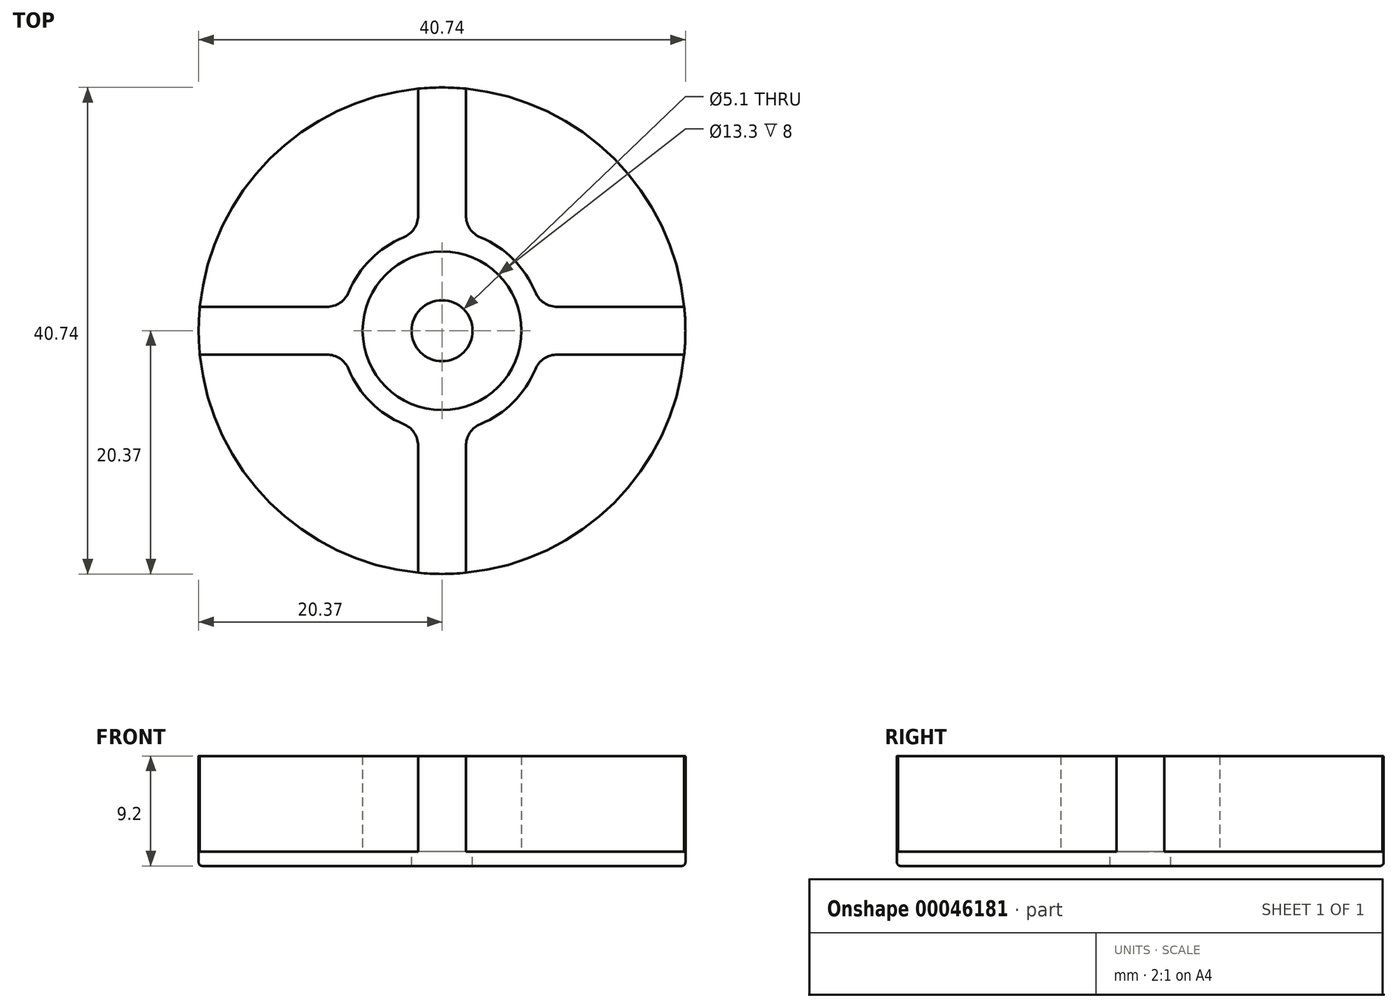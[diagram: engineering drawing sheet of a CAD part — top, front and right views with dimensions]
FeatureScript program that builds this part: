
annotation { "Feature Type Name" : "Feature", "Feature Type Description" : "" }
export const myFeature = defineFeature(function(context is Context, id is Id, definition is map)
    precondition{}
    {
        {
            var Q0;
            Q0=qCreatedBy(makeId("Top.planeOp"),FACE);
            var sketch = newSketch(context, id + "F0", { "sketchPlane" : qUnion([Q0])});
            skCircle(sketch, "E0", {"center": v(0, 0) * mm, "radius": 20.37 * mm});
            skLineSegment(sketch, "E1", {"start": v(0, 0) * mm, "end": v(0, 20.37) * mm, "construction": true});
            skLineSegment(sketch, "E2", {"start": v(0, 0) * mm, "end": v(2, 20.27) * mm, "construction": true});
            skLineSegment(sketch, "E3", {"start": v(7.8, 18.82) * mm, "end": v(0, 0) * mm, "construction": true});
            skLineSegment(sketch, "E4", {"start": v(0, 0) * mm, "end": v(14.4, 14.4) * mm, "construction": true});
            skLineSegment(sketch, "E5", {"start": v(2, 20.27) * mm, "end": v(2, 9.65) * mm});
            skLineSegment(sketch, "E6", {"start": v(0, 0) * mm, "end": v(3.97, 19.98) * mm, "construction": true});
            skLineSegment(sketch, "E7.MirrorCS", {"start": v(20.27, 2) * mm, "end": v(9.65, 2) * mm});
            skPoint(sketch, "E8.newPointA", {"position": v(-1.41, 1.41) * mm});
            skPoint(sketch, "E8.newPointB", {"position": v(2, 0) * mm});
            skArc(sketch, "E8.filletArc", {"start": v(2, 9.65) * mm, "mid": v(2.34, 8.54) * mm, "end": v(3.23, 7.8) * mm});
            skPoint(sketch, "E9.newPointA", {"position": v(1.41, -1.41) * mm});
            skPoint(sketch, "E9.newPointB", {"position": v(0, 2) * mm});
            skArc(sketch, "E9.filletArc", {"start": v(7.8, 3.23) * mm, "mid": v(8.54, 2.34) * mm, "end": v(9.65, 2) * mm});
            skLineSegment(sketch, "E10.MirrorCS", {"start": v(20.27, -2) * mm, "end": v(9.65, -2) * mm});
            skArc(sketch, "E11.MirrorCS", {"start": v(7.8, -3.23) * mm, "mid": v(8.54, -2.34) * mm, "end": v(9.65, -2) * mm});
            skArc(sketch, "E12.MirrorCS", {"start": v(2, -9.65) * mm, "mid": v(2.34, -8.54) * mm, "end": v(3.23, -7.8) * mm});
            skLineSegment(sketch, "E13.MirrorCS", {"start": v(2, -20.27) * mm, "end": v(2, -9.65) * mm});
            skLineSegment(sketch, "E14.MirrorCS", {"start": v(-2, 20.27) * mm, "end": v(-2, 9.65) * mm});
            skArc(sketch, "E15.MirrorCS", {"start": v(-2, 9.65) * mm, "mid": v(-2.34, 8.54) * mm, "end": v(-3.23, 7.8) * mm});
            skArc(sketch, "E16.MirrorCS", {"start": v(-7.8, 3.23) * mm, "mid": v(-8.54, 2.34) * mm, "end": v(-9.65, 2) * mm});
            skLineSegment(sketch, "E17.MirrorCS", {"start": v(-20.27, 2) * mm, "end": v(-9.65, 2) * mm});
            skLineSegment(sketch, "E18.MirrorCS", {"start": v(-20.27, -2) * mm, "end": v(-9.65, -2) * mm});
            skArc(sketch, "E19.MirrorCS", {"start": v(-7.8, -3.23) * mm, "mid": v(-8.54, -2.34) * mm, "end": v(-9.65, -2) * mm});
            skArc(sketch, "E20.MirrorCS", {"start": v(-2, -9.65) * mm, "mid": v(-2.34, -8.54) * mm, "end": v(-3.23, -7.8) * mm});
            skLineSegment(sketch, "E21.MirrorCS", {"start": v(-2, -20.27) * mm, "end": v(-2, -9.65) * mm});
            skCircle(sketch, "E22.0", {"center": v(0, 0) * mm, "radius": 6.65 * mm});
            skArc(sketch, "E23", {"start": v(-3.23, 7.8) * mm, "mid": v(-5.97, 5.97) * mm, "end": v(-7.8, 3.23) * mm});
            skPoint(sketch, "E24.orphan", {"position": v(-5.41, 8.24) * mm});
            skPoint(sketch, "E25.MirrorCS.start.orphan", {"position": v(-12.92, 15.75) * mm});
            skPoint(sketch, "E26.MirrorCS.end.orphan", {"position": v(-8.24, 5.41) * mm});
            skPoint(sketch, "E26.MirrorCS.start.orphan", {"position": v(-15.75, 12.92) * mm});
            skPoint(sketch, "E27.MirrorCS.end.orphan", {"position": v(5.41, 8.24) * mm});
            skPoint(sketch, "E27.MirrorCS.start.orphan", {"position": v(12.92, 15.75) * mm});
            skPoint(sketch, "E28.MirrorCS.end.orphan", {"position": v(-8.24, -5.41) * mm});
            skPoint(sketch, "E28.MirrorCS.start.orphan", {"position": v(-15.75, -12.92) * mm});
            skPoint(sketch, "E29.MirrorCS.end.orphan", {"position": v(-5.41, -8.24) * mm});
            skPoint(sketch, "E29.MirrorCS.start.orphan", {"position": v(-12.92, -15.75) * mm});
            skArc(sketch, "E30.trimOffspring", {"start": v(-7.8, -3.23) * mm, "mid": v(-5.97, -5.97) * mm, "end": v(-3.23, -7.8) * mm});
            skArc(sketch, "E31.trimOffspring", {"start": v(3.23, -7.8) * mm, "mid": v(5.97, -5.97) * mm, "end": v(7.8, -3.23) * mm});
            skPoint(sketch, "E32.orphan", {"position": v(5.41, -8.24) * mm});
            skPoint(sketch, "E33.MirrorCS.start.orphan", {"position": v(12.92, -15.75) * mm});
            skPoint(sketch, "E34.orphan", {"position": v(8.24, -5.41) * mm});
            skPoint(sketch, "E35.MirrorCS.start.orphan", {"position": v(15.75, -12.92) * mm});
            skPoint(sketch, "E36.MirrorCS.end.orphan", {"position": v(8.24, 5.41) * mm});
            skPoint(sketch, "E36.MirrorCS.start.orphan", {"position": v(15.75, 12.92) * mm});
            skArc(sketch, "E37.trimOffspring", {"start": v(7.8, 3.23) * mm, "mid": v(5.97, 5.97) * mm, "end": v(3.23, 7.8) * mm});
            skCircle(sketch, "E38", {"center": v(0, 0) * mm, "radius": 2.55 * mm});
            skSolve(sketch);
        }
        {
            var Q0;
            {var subQ1=sQuery(id+"F0.wireOp",EDGE,"E7.MirrorCS");Q0=makeQuery(id+"F0.imprint","IMPRINT",FACE,{"disambiguationData":[TD([[makeQuery(id+"F0.imprint","IMPRINT",EDGE,{"derivedFrom":subQ1}),-1.0]])]});}
            var Q1;
            {var subQ1=sQuery(id+"F0.wireOp",EDGE,"E5");Q1=makeQuery(id+"F0.imprint","IMPRINT",FACE,{"disambiguationData":[TD([[makeQuery(id+"F0.imprint","IMPRINT",EDGE,{"derivedFrom":subQ1}),1.0]])]});}
            var Q2;
            {var subQ1=sQuery(id+"F0.wireOp",EDGE,"E14.MirrorCS");Q2=makeQuery(id+"F0.imprint","IMPRINT",FACE,{"disambiguationData":[TD([[makeQuery(id+"F0.imprint","IMPRINT",EDGE,{"derivedFrom":subQ1}),-1.0]])]});}
            var Q3;
            {var subQ1=sQuery(id+"F0.wireOp",EDGE,"E18.MirrorCS");Q3=makeQuery(id+"F0.imprint","IMPRINT",FACE,{"disambiguationData":[TD([[makeQuery(id+"F0.imprint","IMPRINT",EDGE,{"derivedFrom":subQ1}),-1.0]])]});}
            var Q4;
            {var subQ1=sQuery(id+"F0.wireOp",EDGE,"E29.MirrorCS");Q4=makeQuery(id+"F0.imprint","IMPRINT",FACE,{"disambiguationData":[TD([[makeQuery(id+"F0.imprint","IMPRINT",EDGE,{"derivedFrom":subQ1}),-1.0]])]});}
            var Q5;
            {var subQ0=sQuery(id+"F0.wireOp",EDGE,"E33.MirrorCS");Q5=makeQuery(id+"F0.imprint","IMPRINT",FACE,{"disambiguationData":[TD([[makeQuery(id+"F0.imprint","IMPRINT",EDGE,{"derivedFrom":subQ0}),1.0]])]});}
            var Q6;
            {var subQ1=sQuery(id+"F0.wireOp",EDGE,"E10.MirrorCS");Q6=makeQuery(id+"F0.imprint","IMPRINT",FACE,{"disambiguationData":[TD([[makeQuery(id+"F0.imprint","IMPRINT",EDGE,{"derivedFrom":subQ1}),1.0]])]});}
            var Q7;
            {var subQ10=sQuery(id+"F0.wireOp",EDGE,"E5");Q7=makeQuery(id+"F0.imprint","IMPRINT",FACE,{"disambiguationData":[TD([[makeQuery(id+"F0.imprint","IMPRINT",EDGE,{"derivedFrom":subQ10}),-1.0]])]});}
            var Q8;
            {var subQ1=sQuery(id+"F0.wireOp",EDGE,"E26.MirrorCS");Q8=makeQuery(id+"F0.imprint","IMPRINT",FACE,{"disambiguationData":[TD([[makeQuery(id+"F0.imprint","IMPRINT",EDGE,{"derivedFrom":subQ1}),-1.0]])]});}
            var Q9;
            Q9=makeQuery(id+"F0.imprint","IMPRINT",FACE,{"disambiguationData":[TD([[makeQuery(id+"F0.imprint","IMPRINT",EDGE,{"derivedFrom":sQuery(id+"F0.wireOp",EDGE,"E22.0")}),1.0]])]});
            extrude(context, id + "F1", {"entities" : qUnion([Q0, Q1, Q2, Q3, Q4, Q5, Q6, Q7, Q8, Q9]), "oppositeDirection" : true, "depth" : 1.2 * mm});
        }
        {
            var Q0;
            {var subQ10=sQuery(id+"F0.wireOp",EDGE,"E5");Q0=makeQuery(id+"F0.imprint","IMPRINT",FACE,{"disambiguationData":[TD([[makeQuery(id+"F0.imprint","IMPRINT",EDGE,{"derivedFrom":subQ10}),-1.0]])]});}
            extrude(context, id + "F2", {"entities" : qUnion([Q0]), "operationType" : NewBodyOperationType.ADD, "depth" : 8 * mm});
        }
        {
            var Q0;
            Q0=makeQuery(id+"F1.opExtrude","CAP_EDGE",EDGE,{"disambiguationData":[OSD([sQuery(id+"F0.wireOp",EDGE,"E0")])],"isStart":false});
            fillet(context, id + "F3", {"entities" : qUnion([Q0]), "radius" : .3 * mm, "tangentPropagation" : true, "allowEdgeOverflow" : false});
        }
    });
